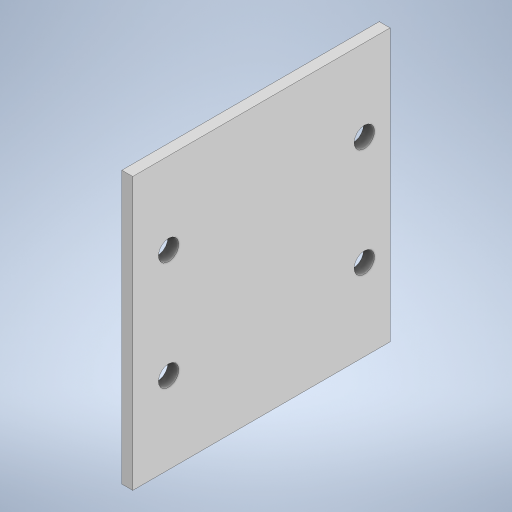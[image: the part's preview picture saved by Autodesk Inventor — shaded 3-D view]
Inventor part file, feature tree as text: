
AUTODESK INVENTOR PART (.ipt)
format: ipt  version: 2023 (Build 270158000, 158)  size: 217,600 bytes
history: native  units: in
note: dims shown in document units (in); Inventor stores cm internally (conversion verified against a paired STEP export)
features: extrude x1, sketch x1
ambient origin geometry x8: Origin, YZ Plane, XZ Plane, XY Plane, X Axis, Y Axis, Z Axis, Center Point
bodies: Solid1 (feature_tree)
feature tree (2):
  extrude  "Extrusion1"  Depth=0.71in
  sketch  "Sketch1"  dims[d0=0.5in d1=0.71in d2=0.75in d3=0.125in d4=0.2812in d5=0.0563in d9=0.54in d10=0.3in d11=0.3in d12=0.54in d13=0.1in d14=0.39in d15=0.125in d17=0.2in d18=0.03in d19=0.0in]
